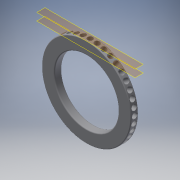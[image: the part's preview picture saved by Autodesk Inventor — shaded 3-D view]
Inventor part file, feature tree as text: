
AUTODESK INVENTOR PART (.ipt)
format: ipt  version: 2018 (Build 220112000, 112)  size: 373,760 bytes
history: native  units: in
note: dims shown in document units (in); Inventor stores cm internally (conversion verified against a paired STEP export)
features: other x13, reference x7, extrude x2, plane x2, fillet x2, sketch x2, pattern_circular x1, chamfer x1
ambient origin geometry x8: Origin, YZ Plane, XZ Plane, XY Plane, X Axis, Y Axis, Z Axis, Center Point
bodies: Solid1 (feature_tree)
feature tree (30):
  extrude  "Extrusion1"  TaperAngle=135.0deg  [1 undecoded]
  plane  "Work Plane2"
  extrude  "Extrusion2"  Depth=2.0in
  pattern_circular  "Circular Pattern1"  [2 undecoded]
  chamfer  "Chamfer1"  Distance=14.0in
  fillet  "Fillet1"  [1 undecoded]
  fillet  "Fillet2"  Radius=14.0in
  sketch  "Sketch1"  dims[d0=45.0deg d1=135.0deg]
  reference  "Reference1"
  reference  "Reference2"
  reference  "Reference3"
  reference  "Reference4"
  reference  "Reference5"
  reference  "Reference6"
  plane  "Work Plane1"
  sketch  "Sketch2"  dims[d2=45.0deg d3=12.0in d4=12.0in d5=14.0in d6=0.0in d7=-14.0in d8=14.0in d9=0.0in d10=15.748in d11=360.0deg d13=1.0in d14=0.125in d15=45.0deg d16=1.0in d17=2.0in]
  reference  "Reference7"
  other  "Assembly4"
  other  "FullArmAJB:25"
  other  "FullRadiusPoleAJB:1"
  other  "1_6RadiusPole_WithBolt_AJB:1"
  other  "1_6RadiusPoleAJB:1"
  other  "FullArmAJB:35"
  other  "FullArmAJB:38"
  other  "FullArmAJB:36"
  other  "FullArmAJB:26"
  other  "FullArmAJB:6"
  other  "FullArmAJB:31"
  other  "FullRadiusPoleAJB:2"
  other  "1_6RadiusPole_WithBolt_AJB:4"
note: 4 required parameter values undecoded (feature->parameter linkage not recoverable at this tier; creation-order binding heuristic only, values carry confidence <= 0.55)
